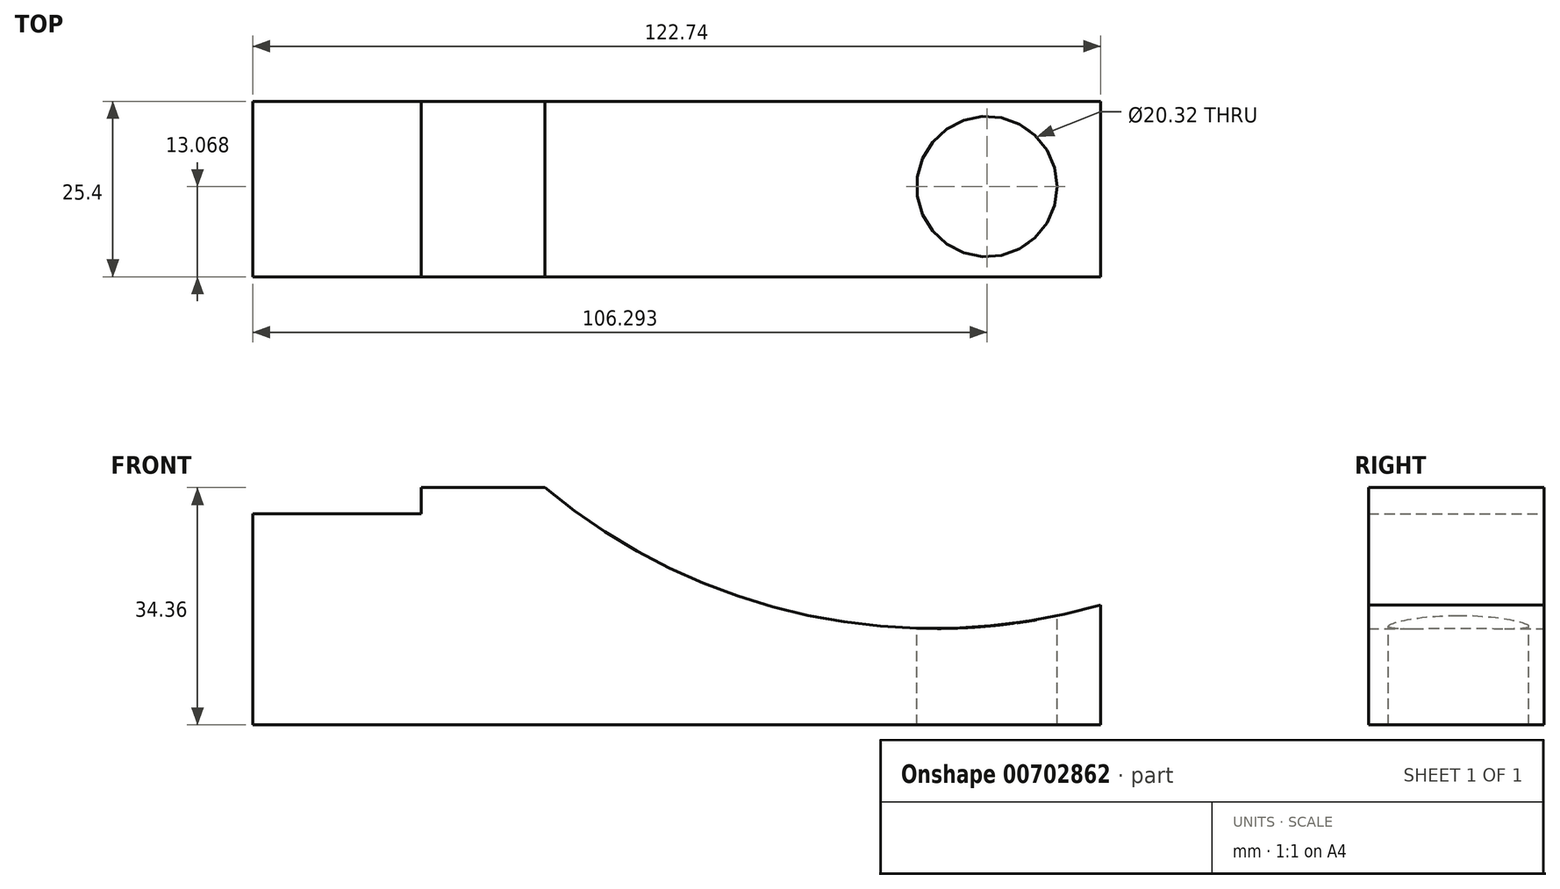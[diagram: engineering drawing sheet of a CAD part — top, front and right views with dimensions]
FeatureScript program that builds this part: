
annotation { "Feature Type Name" : "Feature", "Feature Type Description" : "" }
export const myFeature = defineFeature(function(context is Context, id is Id, definition is map)
    precondition{}
    {
        {
            var Q0;
            Q0=qCreatedBy(makeId("Front.planeOp"),FACE);
            var sketch = newSketch(context, id + "F0", { "sketchPlane" : qUnion([Q0])});
            skLineSegment(sketch, "E0", {"start": v(-68.27, -30.54) * mm, "end": v(54.47, -30.54) * mm});
            skLineSegment(sketch, "E1", {"start": v(54.47, -30.54) * mm, "end": v(54.47, -13.21) * mm});
            skLineSegment(sketch, "E2", {"start": v(-25.98, 3.82) * mm, "end": v(-43.9, 3.82) * mm});
            skLineSegment(sketch, "E3", {"start": v(-43.9, 3.82) * mm, "end": v(-43.9, 0) * mm});
            skLineSegment(sketch, "E4", {"start": v(-43.9, 0) * mm, "end": v(-68.27, 0) * mm});
            skLineSegment(sketch, "E5", {"start": v(-68.27, 0) * mm, "end": v(-68.27, -30.54) * mm});
            skArc(sketch, "E6", {"start": v(-25.98, 3.82) * mm, "mid": v(12.13, -14.69) * mm, "end": v(54.47, -13.21) * mm});
            skSolve(sketch);
        }
        {
            var Q0;
            Q0 = qSketchRegion(id + "F0", true);
            extrude(context, id + "F1", {"entities" : qUnion([Q0]), "depth" : 25.4 * mm, "offsetDistance" : 25.4 * mm});
        }
        {
            var Q0;
            Q0=qCreatedBy(makeId("Top.planeOp"),FACE);
            var sketch = newSketch(context, id + "F2", { "sketchPlane" : qUnion([Q0])});
            skCircle(sketch, "E7", {"center": v(38.02, -12.33) * mm, "radius": 6.85 * mm});
            skSolve(sketch);
        }
        {
            var Q0;
            Q0=sQuery(id+"F2.wireOp",VERTEX,"E7.center");
            var Q1;
            Q1=makeQuery(id+"F1.opExtrude","SWEPT_BODY",BODY,{"disambiguationData":[OSD([sQuery(id+"F0.wireOp",EDGE,"E0"),sQuery(id+"F0.wireOp",EDGE,"E1"),sQuery(id+"F0.wireOp",EDGE,"E2"),sQuery(id+"F0.wireOp",EDGE,"E3"),sQuery(id+"F0.wireOp",EDGE,"E4"),sQuery(id+"F0.wireOp",EDGE,"E5"),sQuery(id+"F0.wireOp",EDGE,"E6")])]});
            hole(context, id + "F3", {"style" : HoleStyle.SIMPLE, "endStyle" : HoleEndStyle.THROUGH, "holeDiameter" : 20.32 * mm, "majorDiameter" : 6.35 * mm, "isTappedThrough" : true, "tappedDepth" : 12.7 * mm, "tapClearance" : 3, "locations" : qUnion([Q0]), "scope" : qUnion([Q1])});
        }
    });
